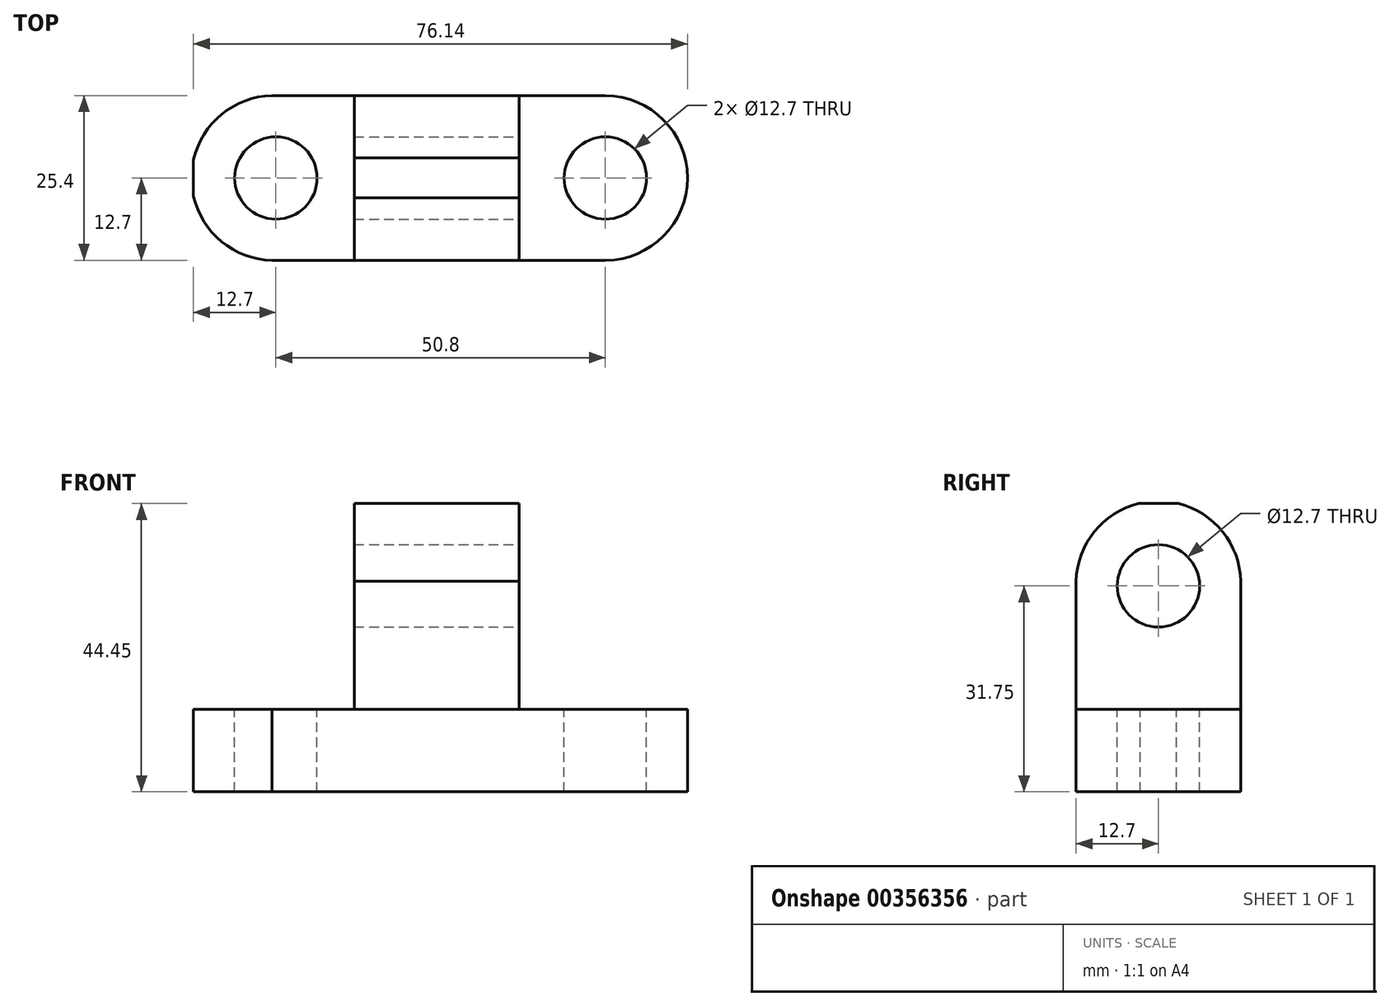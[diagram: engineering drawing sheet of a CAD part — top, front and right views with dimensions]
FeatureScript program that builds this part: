
annotation { "Feature Type Name" : "Feature", "Feature Type Description" : "" }
export const myFeature = defineFeature(function(context is Context, id is Id, definition is map)
    precondition{}
    {
        {
            var Q0;
            Q0=qCreatedBy(makeId("Front.planeOp"),FACE);
            var sketch = newSketch(context, id + "F0", { "sketchPlane" : qUnion([Q0])});
            skLineSegment(sketch, "E0.bottom", {"start": v(-35.52, 0) * mm, "end": v(40.68, 0) * mm});
            skLineSegment(sketch, "E0.top", {"start": v(-35.52, 12.7) * mm, "end": v(40.68, 12.7) * mm});
            skLineSegment(sketch, "E0.left", {"start": v(-35.52, 0) * mm, "end": v(-35.52, 12.7) * mm});
            skLineSegment(sketch, "E0.right", {"start": v(40.68, 0) * mm, "end": v(40.68, 12.7) * mm});
            skSolve(sketch);
        }
        {
            var Q0;
            Q0 = qSketchRegion(id + "F0", true);
            extrude(context, id + "F1", {"entities" : qUnion([Q0]), "depth" : 25.4 * mm});
        }
        {
            var Q0;
            Q0=makeQuery(id+"F1.opExtrude","SWEPT_FACE",FACE,{"disambiguationData":[OSD([sQuery(id+"F0.wireOp",EDGE,"E0.top")])]});
            var sketch = newSketch(context, id + "F2", { "sketchPlane" : qUnion([Q0])});
            skCircle(sketch, "E1", {"center": v(-22.82, -12.7) * mm, "radius": 6.35 * mm});
            skCircle(sketch, "E2", {"center": v(27.98, -12.7) * mm, "radius": 6.35 * mm});
            skArc(sketch, "E3", {"start": v(-22.82, 0) * mm, "mid": v(-35.83, -12.7) * mm, "end": v(-22.82, -25.4) * mm});
            skArc(sketch, "E4", {"start": v(27.98, -25.4) * mm, "mid": v(40.62, -12.7) * mm, "end": v(27.98, 0) * mm});
            skSolve(sketch);
        }
        {
            var Q0;
            Q0=makeQuery(id+"F2.imprint","IMPRINT",FACE,{"disambiguationData":[TD([[makeQuery(id+"F2.imprint","IMPRINT",EDGE,{"derivedFrom":sQuery(id+"F2.wireOp",EDGE,"E1")}),1.0]])]});
            var Q1;
            Q1=makeQuery(id+"F2.imprint","IMPRINT",FACE,{"disambiguationData":[TD([[makeQuery(id+"F2.imprint","IMPRINT",EDGE,{"derivedFrom":sQuery(id+"F2.wireOp",EDGE,"E2")}),1.0]])]});
            var Q2;
            {var subQ0=sQuery(id+"F2.wireOp",EDGE,"E4");Q2=makeQuery(id+"F2.imprint","IMPRINT",FACE,{"disambiguationData":[TD([[makeQuery(id+"F2.imprint","IMPRINT",EDGE,{"derivedFrom":subQ0}),-1.0]])]});}
            var Q3;
            {var subQ0=sQuery(id+"F2.wireOp",EDGE,"E3");var subQ1=sQuery(id+"F0.wireOp",EDGE,"E0.top");var subQ2=makeQuery(id+"F1.opExtrude","CAP_EDGE",EDGE,{"disambiguationData":[OSD([subQ1])],"isStart":true});var subQ3=makeQuery(id+"F2.imprint","INTERSECT",VERTEX,{"disambiguationData":[OD(1.0)],"derivedFrom":[subQ2,subQ0]});Q3=makeQuery(id+"F2.imprint","IMPRINT",FACE,{"disambiguationData":[TD([[makeQuery(id+"F2.imprint","IMPRINT",EDGE,{"disambiguationData":[TD([[subQ3,-1.0]])],"derivedFrom":subQ0}),-1.0]])]});}
            var Q4;
            {var subQ0=sQuery(id+"F2.wireOp",EDGE,"E3");var subQ1=sQuery(id+"F0.wireOp",EDGE,"E0.top");var subQ4=makeQuery(id+"F1.opExtrude","CAP_EDGE",EDGE,{"disambiguationData":[OSD([subQ1])],"isStart":false});var subQ5=makeQuery(id+"F2.imprint","INTERSECT",VERTEX,{"disambiguationData":[OD(1.0)],"derivedFrom":[subQ4,subQ0]});Q4=makeQuery(id+"F2.imprint","IMPRINT",FACE,{"disambiguationData":[TD([[makeQuery(id+"F2.imprint","IMPRINT",EDGE,{"disambiguationData":[TD([[subQ5,1.0]])],"derivedFrom":subQ0}),-1.0]])]});}
            extrude(context, id + "F3", {"entities" : qUnion([Q0, Q1, Q2, Q3, Q4]), "operationType" : NewBodyOperationType.REMOVE, "oppositeDirection" : true, "depth" : 12.7 * mm});
        }
        {
            var Q0;
            Q0=makeQuery(id+"F1.opExtrude","CAP_FACE",FACE,{"disambiguationData":[OSD([sQuery(id+"F0.wireOp",EDGE,"E0.bottom"),sQuery(id+"F0.wireOp",EDGE,"E0.top"),sQuery(id+"F0.wireOp",EDGE,"E0.left"),sQuery(id+"F0.wireOp",EDGE,"E0.right")])],"isStart":false});
            var sketch = newSketch(context, id + "F4", { "sketchPlane" : qUnion([Q0])});
            skLineSegment(sketch, "E5.bottom", {"start": v(-10.73, 12.7) * mm, "end": v(14.67, 12.7) * mm});
            skLineSegment(sketch, "E5.top", {"start": v(-10.73, 44.45) * mm, "end": v(14.67, 44.45) * mm});
            skLineSegment(sketch, "E5.left", {"start": v(-10.73, 12.7) * mm, "end": v(-10.73, 44.45) * mm});
            skLineSegment(sketch, "E5.right", {"start": v(14.67, 12.7) * mm, "end": v(14.67, 44.45) * mm});
            skSolve(sketch);
        }
        {
            var Q0;
            Q0=makeQuery(id+"F4.imprint","IMPRINT",FACE,{"disambiguationData":[TD([[makeQuery(id+"F4.imprint","IMPRINT",EDGE,{"derivedFrom":sQuery(id+"F4.wireOp",EDGE,"E5.bottom")}),1.0]])]});
            extrude(context, id + "F5", {"entities" : qUnion([Q0]), "oppositeDirection" : true, "depth" : 25.4 * mm});
        }
        {
            var Q0;
            Q0=makeQuery(id+"F5.opExtrude","SWEPT_FACE",FACE,{"disambiguationData":[OSD([sQuery(id+"F4.wireOp",EDGE,"E5.right")])]});
            var sketch = newSketch(context, id + "F6", { "sketchPlane" : qUnion([Q0])});
            skCircle(sketch, "E6", {"center": v(-12.7, 31.75) * mm, "radius": 6.35 * mm});
            skArc(sketch, "E7", {"start": v(0, 31.75) * mm, "mid": v(-12.7, 44.83) * mm, "end": v(-25.4, 31.75) * mm});
            skSolve(sketch);
        }
        {
            var Q0;
            Q0=makeQuery(id+"F6.imprint","IMPRINT",FACE,{"disambiguationData":[TD([[makeQuery(id+"F6.imprint","IMPRINT",EDGE,{"derivedFrom":sQuery(id+"F6.wireOp",EDGE,"E6")}),1.0]])]});
            var Q1;
            {var subQ0=sQuery(id+"F6.wireOp",EDGE,"E7");var subQ1=sQuery(id+"F4.wireOp",EDGE,"E5.right");var subQ2=makeQuery(id+"F5.opExtrude","CAP_EDGE",EDGE,{"disambiguationData":[OSD([subQ1])],"isStart":false});var subQ3=makeQuery(id+"F6.imprint","INTERSECT",VERTEX,{"disambiguationData":[OD(1.0)],"derivedFrom":[subQ2,subQ0]});Q1=makeQuery(id+"F6.imprint","IMPRINT",FACE,{"disambiguationData":[TD([[makeQuery(id+"F6.imprint","IMPRINT",EDGE,{"disambiguationData":[TD([[subQ3,-1.0]])],"derivedFrom":subQ0}),-1.0]])]});}
            var Q2;
            {var subQ0=sQuery(id+"F6.wireOp",EDGE,"E7");var subQ1=sQuery(id+"F4.wireOp",EDGE,"E5.right");var subQ4=makeQuery(id+"F5.opExtrude","CAP_EDGE",EDGE,{"disambiguationData":[OSD([subQ1])],"isStart":true});var subQ5=makeQuery(id+"F6.imprint","INTERSECT",VERTEX,{"disambiguationData":[OD(1.0)],"derivedFrom":[subQ4,subQ0]});Q2=makeQuery(id+"F6.imprint","IMPRINT",FACE,{"disambiguationData":[TD([[makeQuery(id+"F6.imprint","IMPRINT",EDGE,{"disambiguationData":[TD([[subQ5,1.0]])],"derivedFrom":subQ0}),-1.0]])]});}
            extrude(context, id + "F7", {"entities" : qUnion([Q0, Q1, Q2]), "operationType" : NewBodyOperationType.REMOVE, "oppositeDirection" : true, "depth" : 25.4 * mm});
        }
    });
